FCSTD DOCUMENT  (FreeCAD 0.18R15518 (Git))
Label: kunda1-thingy-sketcher
License: All rights reserved
LicenseURL: http://en.wikipedia.org/wiki/All_rights_reserved
objects: Sketcher::SketchObject×1
note: 1 computed .brp shape members not serialized (recipe doc carries the construction recipe); baked Part::Feature solids carry a one-line shape summary decoded from their .brp

FEATURE [Sketcher::SketchObject] Sketch
  sketch-geometry (14):
    g0: LineSegment StartX=17.6248 StartY=80.6079 StartZ=0 EndX=-60.9961 EndY=55.5675 EndZ=0
    g1: LineSegment StartX=-60.9961 StartY=55.5675 StartZ=0 EndX=-78.6209 EndY=-25.0404 EndZ=0
    g2: LineSegment StartX=-78.6209 StartY=-25.0404 StartZ=0 EndX=-17.6248 EndY=-80.6079 EndZ=0
    g3: LineSegment StartX=-17.6248 StartY=-80.6079 StartZ=0 EndX=60.9961 EndY=-55.5675 EndZ=0
    g4: LineSegment StartX=60.9961 StartY=-55.5675 StartZ=0 EndX=78.6209 EndY=25.0404 EndZ=0
    g5: LineSegment StartX=78.6209 StartY=25.0404 StartZ=0 EndX=17.6248 EndY=80.6079 EndZ=0
    g6: Circle [constr] CenterX=0 CenterY=0 CenterZ=0 NormalX=0 NormalY=0 NormalZ=1 AngleXU=0 Radius=82.5122
    g7: LineSegment StartX=-24.9221 StartY=-7.93758 StartZ=0 EndX=-16.404 EndY=-75.0245 EndZ=0
    g8: LineSegment StartX=-16.404 StartY=-75.0245 StartZ=0 EndX=37.436 EndY=-34.1042 EndZ=0
    g9: LineSegment StartX=37.436 StartY=-34.1042 StartZ=0 EndX=-24.9221 EndY=-7.93758 EndZ=0
    g10: Circle [constr] CenterX=-1.29669 CenterY=-39.0221 CenterZ=0 NormalX=0 NormalY=0 NormalZ=1 AngleXU=0 Radius=39.0436
    g11: LineSegment [constr] StartX=60.9961 StartY=-55.5675 StartZ=0 EndX=-60.9961 EndY=55.5675 EndZ=0
    g12: LineSegment [constr] StartX=-78.6209 StartY=-25.0404 StartZ=0 EndX=78.6209 EndY=25.0404 EndZ=0
    g13: LineSegment [constr] StartX=-17.6248 StartY=-80.6079 StartZ=0 EndX=17.6248 EndY=80.6079 EndZ=0
  constraints (33):
    c: Coincident(g0,g1)
    c: Coincident(g1,g2)
    c: Coincident(g2,g3)
    c: Coincident(g3,g4)
    c: Coincident(g4,g5)
    c: Coincident(g5,g0)
    c: Equal(g0, g1-g5) x5
    c: PointOnObject(g0,g6)
    c: PointOnObject(g1,g6)
    c: PointOnObject(g2,g6)
    c: PointOnObject(g3,g6)
    c: PointOnObject(g4,g6)
    c: PointOnObject(g5,g6)
    c: Coincident(g7,g8)
    c: Coincident(g8,g9)
    c: Coincident(g9,g7)
    c: Equal(g7,g8)
    c: Equal(g7,g9)
    c: PointOnObject(g7,g10)
    c: PointOnObject(g8,g10)
    c: PointOnObject(g9,g10)
    c: Coincident(g13,g2)
    c: Coincident(g13,g0)
    c: Coincident(g11,g0)
    c: Coincident(g11,g3)
    c: Coincident(g12,g4)
    c: Coincident(g12,g1)
    c: Radius(g6) = 82.5122
    c: Coincident(g6,g-1)
    c: PointOnObject(g7,g13)
    c: PointOnObject(g8,g11)
    c: DistanceX(g10) = -1.29669
    c: DistanceY(g10) = -39.0221
